# Revit family: CENTUM Spannschloss DIN1478 Stahl
name_source: partatom
category: HLS-Bauteile
revit_build: Autodesk Revit 2017 (Build: 20190507_1515(x64)
units: mm (PartAtom-declared; Revit-internal decimal feet)

## family parameters
Arbeitsebenenbasiert = Ja
Beim Laden mit Abzugskörper schneiden = Nein
Bemaßung runder Anschluss = Durchmesser verwenden
Gemeinsam genutzt = Ja
Immer vertikal = Nein
Raumberechnungspunkt = Nein
Teiletyp = Normal

## types (2) — shared parameters
Fabrikat = MEFA
Firma = MEFA Befestigungs- und Montagesysteme GmbH
Kurztext1 = Spannschloss geschlossen DIN 1478
Lochdurchmesser = 10 mm
Material = Stahl
Mengeneinheit = St
Oberflaeche = galvanisch verzinkt
Vorgabe-Ansicht = 1219 mm
vpe = 1 St

## per-type parameters (varying)
| type | Artikelnummer | Außendurchmesser | EAN | Gewicht | Gewicht pro Bauteil | Gewinde | Kurztext2 | L | Länge | M | Nachstellbarkeit | d1 | d2 | d3 | max. zul. Last |
| CENTUM Spannschloss DIN1478 Stahl M12 | 1660007412 | 25 mm  [stored 0.082021 ft] | 4250928449559 | 0.24 kg | 0.24 kg | M12 | M12 gvz | 125 mm  [stored 0.410105 ft] | 125 mm  [stored 0.410105 ft] | 15 mm  [stored 0.0492126 ft] | 90 mm | 5 mm  [stored 0.0164042 ft] | 9 mm  [stored 0.0295276 ft] | 13 mm | 24.00 kN |
| CENTUM Spannschloss DIN1478 Stahl M16 | 1660007416 | 30 mm  [stored 0.0984252 ft] | 4250928449566 | 0.37 kg | 0.37 kg | M16 | M16 gvz | 170 mm  [stored 0.557743 ft] | 170 mm  [stored 0.557743 ft] | 18 mm  [stored 0.0590551 ft] | 120 mm | 7 mm  [stored 0.0229659 ft] | 12 mm  [stored 0.0393701 ft] | 15 mm  [stored 0.0492126 ft] | 44.00 kN |

note: [stored X ft] marks values corroborated as IEEE doubles in the binary element streams (Revit-internal decimal feet)
